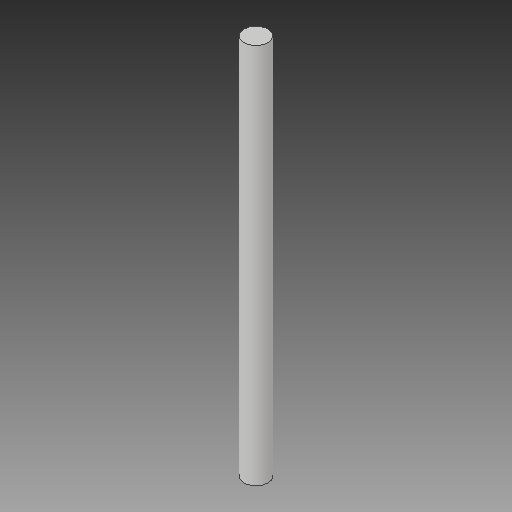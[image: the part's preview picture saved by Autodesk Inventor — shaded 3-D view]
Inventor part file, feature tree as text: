
AUTODESK INVENTOR PART (.ipt)
format: ipt  version: 2017 (Build 210142000, 142)  size: 95,744 bytes
history: native  units: mm
features: other x1, extrude x1, sketch x1
ambient origin geometry x8: Origin, YZ Plane, XZ Plane, XY Plane, X Axis, Y Axis, Z Axis, Center Point
bodies: Body1 (feature_tree)
feature tree (3):
  other  "Sólido1"
  extrude  "Extrusión1"  Depth=160.0mm TaperAngle=0.0deg
  sketch  "Boceto1"  dims[d0=10.0mm d1=160.0mm d2=0.0mm]
